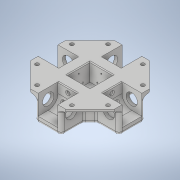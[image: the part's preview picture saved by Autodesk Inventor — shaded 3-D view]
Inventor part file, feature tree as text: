
AUTODESK INVENTOR PART (.ipt)
format: ipt  version: 2020 (Build 240168000, 168)  size: 886,272 bytes
history: native  units: in
note: dims shown in document units (in); Inventor stores cm internally (conversion verified against a paired STEP export)
features: extrude x13, sketch x13, fillet x5, pattern_circular x4, chamfer x4, shell x2
ambient origin geometry x8: Origin, YZ Plane, XZ Plane, XY Plane, X Axis, Y Axis, Z Axis, Center Point
bodies: Solid1 (feature_tree)
feature tree (41):
  extrude  "Extrusion1"  Depth=2.6788in
  extrude  "Extrusion13"  Depth=1.5312in
  fillet  "Fillet2"  Radius=1.5312in
  shell  "Shell3"  Thickness=0.0in
  extrude  "Extrusion14"  Depth=1.5312in TaperAngle=0.0deg
  pattern_circular  "Circular Pattern4"  Count=4 Angle=360.0deg
  extrude  "Extrusion15"  Depth=1.75in
  extrude  "Extrusion16"  Depth=0.2156in
  extrude  "Extrusion17"  Depth=0.2156in
  pattern_circular  "Circular Pattern5"  Count=4 Angle=360.0deg
  sketch  "Sketch20"  dims[d82=0.8811in]
  chamfer  "Chamfer14"  Distance=0.0625in Angle=45.0deg
  chamfer  "Chamfer15"  Distance=0.0625in Angle=45.0deg
  extrude  "Extrusion18"  Depth=0.1in
  extrude  "Extrusion19"  Depth=0.05in
  pattern_circular  "Circular Pattern6"  [2 undecoded]
  extrude  "Extrusion20"  Depth=0.05in TaperAngle=360.0deg
  extrude  "Extrusion21"  Depth=0.05in
  extrude  "Extrusion22"  Depth=0.05in
  shell  "Shell4"  Thickness=0.5in
  extrude  "Extrusion25"  Depth=0.05in
  chamfer  "Chamfer16"  Distance=0.285in
  chamfer  "Chamfer17"  Distance=1.5748in Angle=360.0deg
  fillet  "Fillet5"  Radius=5.0in
  fillet  "Fillet6"  Radius=3.9in
  fillet  "Fillet7"  Radius=3.9in
  extrude  "Extrusion26"  Depth=0.05in TaperAngle=0.0deg
  fillet  "Fillet8"  Radius=0.5in
  pattern_circular  "Circular Pattern7"  [2 undecoded]
  sketch  "Sketch1"  dims[d0=7.0in d1=2.6788in]
  sketch  "Sketch14"  dims[d2=2.0in d3=0.0in d71=1.5312in d72=1.5312in d73=0.0in]
  sketch  "Sketch15"  dims[d74=1.5748in d76=360.0deg d78=1.5312in d79=0.0in]
  sketch  "Sketch16"  dims[d80=0.75in]
  sketch  "Sketch17"  dims[d81=0.25in]
  sketch  "Sketch22"  dims[d83=3.0625in d84=0.0in d85=1.5748in d86=360.0deg]
  sketch  "Sketch23"  dims[d88=1.125in d89=0.0in d90=1.75in]
  sketch  "Sketch25"  dims[d91=1.5in d92=0.0in d100=0.2156in]
  sketch  "Sketch26"  dims[d101=0.2156in d102=0.2156in]
  sketch  "Sketch27"  dims[d103=1.125in d104=0.0in d105=1.5748in d106=360.0deg d144=0.0625in d145=0.125in d146=45.0deg d147=0.0625in d148=0.125in d149=45.0deg]
  sketch  "Sketch30"  dims[d150=3.0in d151=0.0in d152=0.1in]
  sketch  "Sketch31"  dims[d153=0.1in d154=0.1in d155=0.05in d156=0.0in d157=1.5748in d158=360.0deg d160=1.75in d161=0.5in d162=0.5in d163=0.285in d164=0.285in d165=1.5748in d167=360.0deg d169=5.0in d170=0.0in d171=3.9in d172=3.9in d173=0.25in d174=0.0in d175=0.5in d176=0.0in d177=0.75in d178=0.625in d179=0.0in d180=0.875in d181=0.3125in d182=1.25in d183=0.0in d184=0.0in d185=0.375in d189=0.375in d201=90.0deg d202=45.0deg d203=3.3125in d204=0.0in d205=0.0625in d206=0.125in d207=45.0deg d208=0.7656in d209=0.0in d211=0.0in d212=0.5in d213=0.125in d214=45.0deg d215=0.25in d216=0.25in d217=0.1in d218=0.625in d219=1.781in d220=0.0in d221=0.05in d222=1.5748in d223=360.0deg d225=0.05in]
note: 4 required parameter values undecoded (feature->parameter linkage not recoverable at this tier; creation-order binding heuristic only, values carry confidence <= 0.55)
